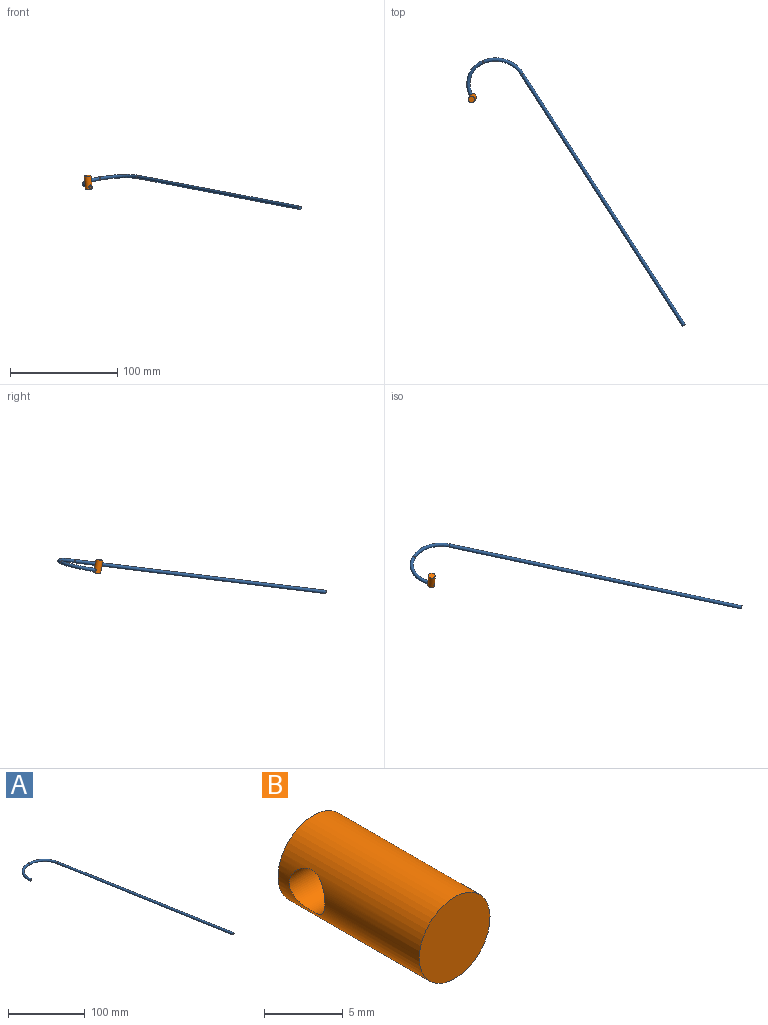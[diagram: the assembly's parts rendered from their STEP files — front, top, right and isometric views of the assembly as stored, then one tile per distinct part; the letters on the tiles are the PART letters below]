
ASSEMBLY  parts=2 mates=1
PART A: 6 faces, bbox 106.2x304.6x3.2 mm
  f0: plane 3.18x3.11mm, normal (0.21,-0.98,0), area 7.9mm2, adj f2
  f1: plane 3.18x3.13mm, normal (0.17,-0.98,0), area 7.9mm2, adj f5
  f2: torus R=22.72mm, axis (0,0,-1), area 403mm2, adj f0,f3
  f3: cylinder r=1.59mm len=3.18mm, axis (1,0,0), area 8.9mm2, adj f2,f4
  f4: torus R=29.21mm, axis (0,0,-1), area 406.8mm2, adj f3,f5
  f5: cylinder r=1.59mm len=276.58mm, axis (0.17,-0.98,0), area 2795.8mm2, adj f1,f4
PART B: 4 faces, bbox 6.4x12.7x6.4 mm
  f0: cylinder r=3.17mm len=12.7mm, axis (0,1,0), area 236.7mm2, adj f1,f2,f3
  f1: plane 6.35x6.35mm, normal (0,-1,0), area 31.7mm2, adj f0
  f2: plane 6.35x6.35mm, normal (0,1,0), area 31.7mm2, adj f0
  f3: cylinder r=1.6mm len=6.35mm, axis (1,0,0), area 59.6mm2, adj f0
PLACE A rot(axis=(0.37,-0.3,0.88),25.2deg) t=(-250.44,21.93,126.33)mm
PLACE B rot(axis=(-0.76,0.46,-0.46),91.9deg) t=(-265.05,1.2,118.31)mm
MATE fastened A.f0 <-> B.f3  axis (0.57,-0.82,-0.1) through (-265.31,0.72,120.86)mm
